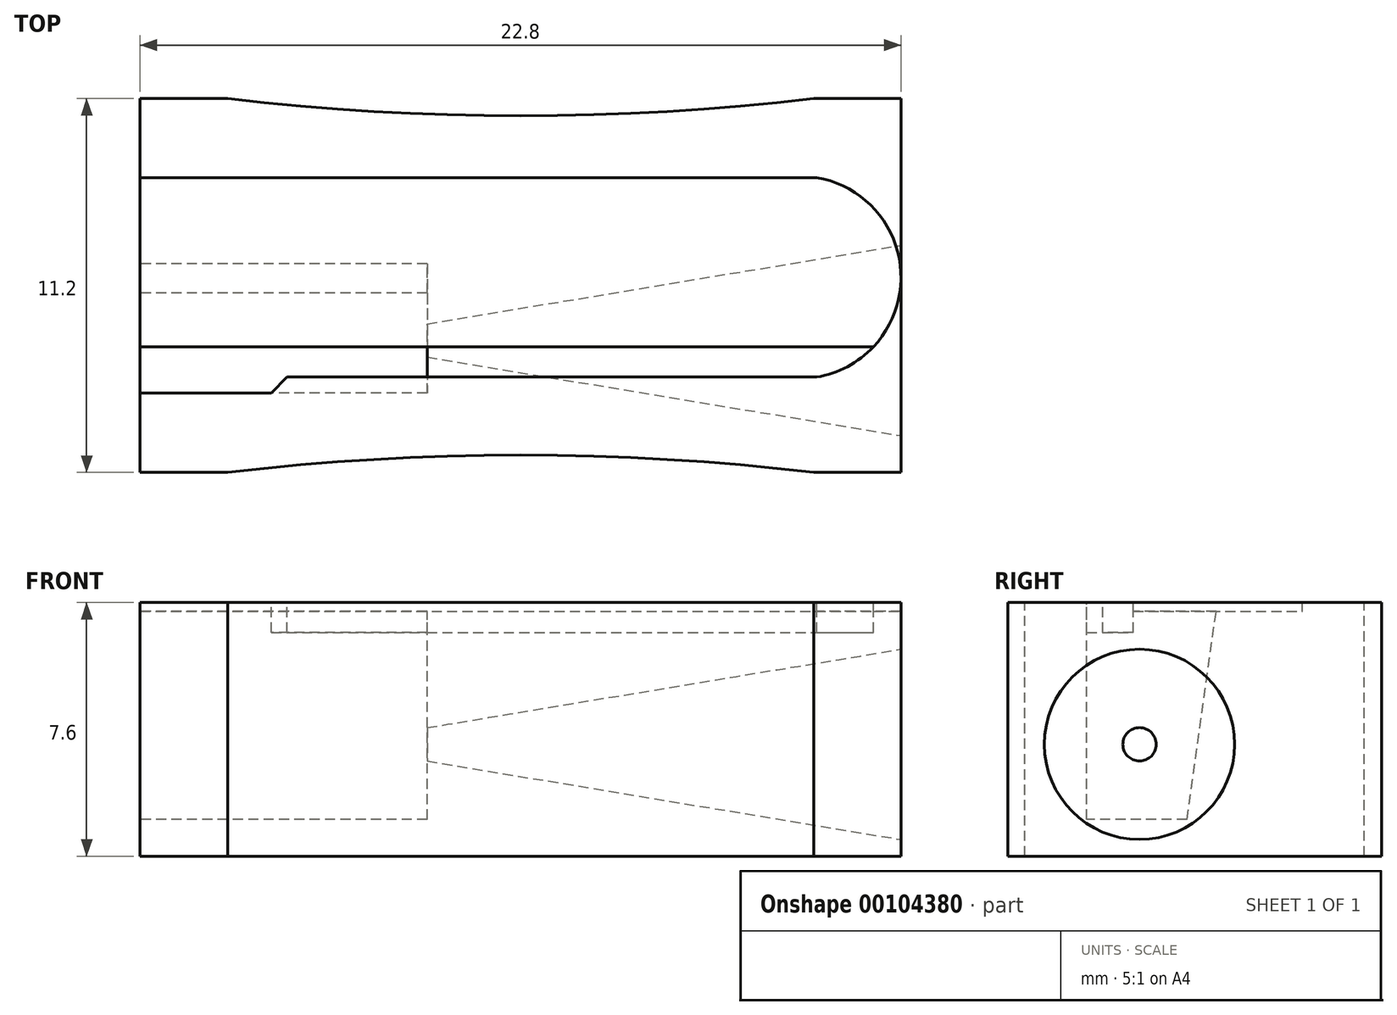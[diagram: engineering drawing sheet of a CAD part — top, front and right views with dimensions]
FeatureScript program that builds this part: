
annotation { "Feature Type Name" : "Feature", "Feature Type Description" : "" }
export const myFeature = defineFeature(function(context is Context, id is Id, definition is map)
    precondition{}
    {
        {
            var Q0;
            Q0=qCreatedBy(makeId("Front.planeOp"),FACE);
            var sketch = newSketch(context, id + "F0", { "sketchPlane" : qUnion([Q0])});
            skLineSegment(sketch, "E0", {"start": v(0, 0) * mm, "end": v(0, 7.6) * mm});
            skLineSegment(sketch, "E1", {"start": v(0, 7.6) * mm, "end": v(22.8, 7.6) * mm});
            skLineSegment(sketch, "E2", {"start": v(22.8, 7.6) * mm, "end": v(22.8, 0) * mm});
            skLineSegment(sketch, "E3", {"start": v(22.8, 0) * mm, "end": v(0, 0) * mm});
            skSolve(sketch);
        }
        {
            var Q0;
            Q0=qSketchRegion(id+"F0",true);
            extrude(context, id + "F1", {"entities" : qUnion([Q0]), "depth" : 11.2 * mm});
        }
        {
            var Q0;
            Q0=makeQuery(id+"F1.opExtrude","SWEPT_FACE",FACE,{"disambiguationData":[OSD([sQuery(id+"F0.wireOp",EDGE,"E2")])]});
            var sketch = newSketch(context, id + "F2", { "sketchPlane" : qUnion([Q0])});
            skCircle(sketch, "E4", {"center": v(-7.25, 3.35) * mm, "radius": 2.85 * mm});
            skSolve(sketch);
        }
        {
            var Q0;
            Q0=makeQuery(id+"F1.opExtrude","CAP_FACE",FACE,{"disambiguationData":[OSD([sQuery(id+"F0.wireOp",EDGE,"E0"),sQuery(id+"F0.wireOp",EDGE,"E1"),sQuery(id+"F0.wireOp",EDGE,"E2"),sQuery(id+"F0.wireOp",EDGE,"E3")])],"isStart":false});
            cPlane(context, id + "F3", {"entities" : qUnion([Q0]), "cplaneType" : CPlaneType.OFFSET, "offset" : 3.95 * mm, "oppositeDirection" : true, "width" : 150 * mm, "height" : 150 * mm});
        }
        {
            var Q0;
            Q0=qCreatedBy(id+"F3.planeOp",FACE);
            var sketch = newSketch(context, id + "F4", { "sketchPlane" : qUnion([Q0])});
            skLineSegment(sketch, "E5", {"start": v(22.8, 0.5) * mm, "end": v(22.8, 3.35) * mm});
            skLineSegment(sketch, "E6", {"start": v(22.8, 3.35) * mm, "end": v(8.6, 3.35) * mm});
            skLineSegment(sketch, "E7", {"start": v(8.6, 3.35) * mm, "end": v(8.6, 2.85) * mm});
            skLineSegment(sketch, "E8", {"start": v(8.6, 2.85) * mm, "end": v(22.8, 0.5) * mm});
            skSolve(sketch);
        }
        {
            var Q0;
            Q0=qSketchRegion(id+"F4",true);
            var Q1;
            Q1=sQuery(id+"F4.wireOp",EDGE,"E6");
            revolve(context, id + "F5", {"operationType" : NewBodyOperationType.REMOVE, "entities" : qUnion([Q0]), "axis" : qUnion([Q1]), "revolveType" : RevolveType.FULL, "oppositeDirection" : true});
        }
        {
            var Q0;
            Q0=makeQuery(id+"F1.opExtrude","SWEPT_FACE",FACE,{"disambiguationData":[OSD([sQuery(id+"F0.wireOp",EDGE,"E1")])]});
            var sketch = newSketch(context, id + "F6", { "sketchPlane" : qUnion([Q0])});
            skLineSegment(sketch, "E9", {"start": v(0, -2.37) * mm, "end": v(20.28, -2.37) * mm});
            skLineSegment(sketch, "E10", {"start": v(0, -2.37) * mm, "end": v(0, -7.44) * mm});
            skLineSegment(sketch, "E11", {"start": v(0, -8.83) * mm, "end": v(3.93, -8.83) * mm});
            skLineSegment(sketch, "E12", {"start": v(3.93, -8.83) * mm, "end": v(4.4, -8.35) * mm});
            skLineSegment(sketch, "E13", {"start": v(4.4, -8.35) * mm, "end": v(20.28, -8.35) * mm});
            skArc(sketch, "E14", {"start": v(20.28, -8.35) * mm, "mid": v(22.8, -5.36) * mm, "end": v(20.28, -2.37) * mm});
            skLineSegment(sketch, "E15", {"start": v(0, -7.44) * mm, "end": v(21.97, -7.44) * mm});
            skLineSegment(sketch, "E16", {"start": v(0, -7.44) * mm, "end": v(0, -8.83) * mm});
            skLineSegment(sketch, "E17", {"start": v(22.8, -11.2) * mm, "end": v(20.18, -11.2) * mm});
            skLineSegment(sketch, "E18", {"start": v(0, -11.2) * mm, "end": v(2.62, -11.2) * mm});
            skArc(sketch, "E19", {"start": v(20.18, -11.2) * mm, "mid": v(11.4, -10.68) * mm, "end": v(2.62, -11.2) * mm});
            skLineSegment(sketch, "E20", {"start": v(2.62, -11.2) * mm, "end": v(20.18, -11.2) * mm});
            skPoint(sketch, "E21.endSnap0", {"position": v(11.4, 0) * mm});
            skLineSegment(sketch, "E22", {"start": v(2.62, 0) * mm, "end": v(20.18, 0) * mm});
            skArc(sketch, "E23", {"start": v(2.62, 0) * mm, "mid": v(11.4, -0.52) * mm, "end": v(20.18, 0) * mm});
            skSolve(sketch);
        }
        {
            var Q0;
            Q0=makeQuery(id+"F6.imprint","IMPRINT",FACE,{"disambiguationData":[TD([[makeQuery(id+"F6.imprint","IMPRINT",EDGE,{"derivedFrom":sQuery(id+"F6.wireOp",EDGE,"E11")}),1.0]])]});
            extrude(context, id + "F7", {"entities" : qUnion([Q0]), "operationType" : NewBodyOperationType.REMOVE, "oppositeDirection" : true, "depth" : 0.9 * mm});
        }
        {
            var Q0;
            Q0=makeQuery(id+"F1.opExtrude","SWEPT_FACE",FACE,{"disambiguationData":[OSD([sQuery(id+"F0.wireOp",EDGE,"E0")])]});
            var sketch = newSketch(context, id + "F8", { "sketchPlane" : qUnion([Q0])});
            skLineSegment(sketch, "E24", {"start": v(5.83, 1.1) * mm, "end": v(8.83, 1.1) * mm});
            skLineSegment(sketch, "E25", {"start": v(8.83, 1.1) * mm, "end": v(8.83, 7.6) * mm});
            skLineSegment(sketch, "E26", {"start": v(5.83, 1.1) * mm, "end": v(4.95, 7.33) * mm});
            skLineSegment(sketch, "E27", {"start": v(4.95, 7.33) * mm, "end": v(8.83, 7.33) * mm});
            skSolve(sketch);
        }
        {
            var Q0;
            {var subQ7=sQuery(id+"F8.wireOp",EDGE,"E24");Q0=makeQuery(id+"F8.imprint","IMPRINT",FACE,{"disambiguationData":[TD([[makeQuery(id+"F8.imprint","IMPRINT",EDGE,{"derivedFrom":subQ7}),1.0]])]});}
            extrude(context, id + "F9", {"entities" : qUnion([Q0]), "operationType" : NewBodyOperationType.REMOVE, "oppositeDirection" : true, "depth" : 8.6 * mm});
        }
        {
            var Q0;
            Q0=makeQuery(id+"F6.imprint","IMPRINT",FACE,{"disambiguationData":[TD([[makeQuery(id+"F6.imprint","IMPRINT",EDGE,{"derivedFrom":sQuery(id+"F6.wireOp",EDGE,"E19")}),1.0]])]});
            extrude(context, id + "F10", {"entities" : qUnion([Q0]), "operationType" : NewBodyOperationType.REMOVE, "oppositeDirection" : true, "depth" : 7.6 * mm});
        }
        {
            var Q0;
            Q0=makeQuery(id+"F6.imprint","IMPRINT",FACE,{"disambiguationData":[TD([[makeQuery(id+"F6.imprint","IMPRINT",EDGE,{"derivedFrom":sQuery(id+"F6.wireOp",EDGE,"E22")}),-1.0]])]});
            extrude(context, id + "F11", {"entities" : qUnion([Q0]), "operationType" : NewBodyOperationType.REMOVE, "oppositeDirection" : true, "depth" : 7.6 * mm});
        }
        {
            var Q0;
            {var subQ1=sQuery(id+"F6.wireOp",EDGE,"E9");Q0=makeQuery(id+"F6.imprint","IMPRINT",FACE,{"disambiguationData":[TD([[makeQuery(id+"F6.imprint","IMPRINT",EDGE,{"derivedFrom":subQ1}),-1.0]])]});}
            extrude(context, id + "F12", {"entities" : qUnion([Q0]), "oppositeDirection" : true, "depth" : 0.27 * mm});
        }
    });
